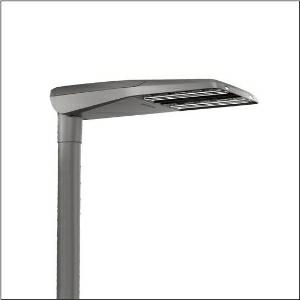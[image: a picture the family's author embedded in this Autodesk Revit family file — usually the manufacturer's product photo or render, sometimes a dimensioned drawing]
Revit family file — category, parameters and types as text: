
# Revit family: streetlight_sl_11_iq_midi___st1_2a_5xc3a51e08le_ac55
name_source: partatom
category: Lighting Fixtures
units: mm (PartAtom-declared; Revit-internal decimal feet)

## family parameters
Cut with Voids When Loaded = No
Host = Face
Light Source = No
Part Type = Normal
Room Calculation Point = No
Round Connector Dimension = Use Diameter
Shared = No

## types (1)
- --- (1 x LED, 9210 lm, 60.4 W, 3000K)
    Apparent Load = 60 VA
    CIE Flux Codes = 32 70 96 100 100
    Color Rendering = 70
    Color Temperature = 3000K
    Default Elevation = 1800 mm
    Description = Streetlight SL 11 iQ midi, mast luminaire, primary light control with 3 zone facetted reflector, of plastic, silver coated, highly specular, primary optical cover: cover, of PMMA, transparent, light distribution: ST1.2a, light emission: direct distribution, primary light characteristic: asymmetric, installation type: post-top, side-entry, LED, High Power LED, rated luminous flux: 9.210lm, luminous efficacy: 153lm/W, light colour: 730, colour temperature: 3000K, control: optimised constant luminous flux control (CLO 2.0), Desk-Remote (wireless, voltage-free reading and setting of iQ features in the workshop via application-optimized NFC function/RFID function), Light-Fading, Smart-Wire, Night-Set, Lumen-Switch, Temp-Guard, Auto-Match, with cable H07RN-F 5x 1.5mm², mains connection: 220..240V, AC, 50/60Hz, connection cable pre-assembled, cable length: 8,5m, start of lifetime: 60W, end of lifetime: 63W, reduction: 30W, luminaire housing, of diecast aluminium, powder-coated, Siteco® metallic grey (DB 702S), length: 780mm, width: 376mm, height: 118mm, spigot size: 60/76mm (post-top) and 42/60/76mm (side-entry), mast flange for spigot size: 42mm: 5XC10008XM4, 60mm: 5XC10008XM2, 76/60mm: 5XC10108XM1, equipment: standard, protection rating (complete): IP66, insulation class (complete): insulation class II (safety insulation), certification: CE, ENEC, VDE, impact resistance: IK09, permissible operating ambient temperature for outdoor applications: -25..+50°C, standard-compliant lighting for roads and squares, packaging unit: 1 piece

Light Distribution: ST1.2a
    Height = 118 mm
    Lamp = 1 x LED
    Lamp Light Flux = 9210 lm
    Lamp Power = 60.4 W
    Lamp count = 1
    Length = 780 mm
    Luminous efficacy = 152 lm/W
    Manufacturer = Siteco
    ModVariant = No
    Model = 5XC3A51E08LE
    Number of Poles = 1
    OnlyDefault = Yes
    Power Factor = 1
    Product Name = Streetlight SL 11 iQ midi | ST1.2a
    Product group = mast luminaire | pylon top
    ProductGroupID = 6100
    Protection Class = Protection class II
    Protection Degree = IP 66
    RLX_Detail_Level = 1
    RlxData = <blob elided: 70205 chars, md5=3eea65a1>
    Socket = socket
    Standby Power = 0 W
    System Light Flux = 9210 lm
    System Power = 60 W
    Type Comments = factory setting: luminous flux: 100 % | dim-lin: 254 | 520 mA
    Type Image = l_1005960.jpg
    URL = http://relux.com
    VarID = @adj_120771
    Voltage = 0 V
    Weight = 0.00 kg
    Width = 376 mm

## geometry (parser evidence)
native form markers: Blend x4, Sweep x11
no freeform markers — native parametric forms only
